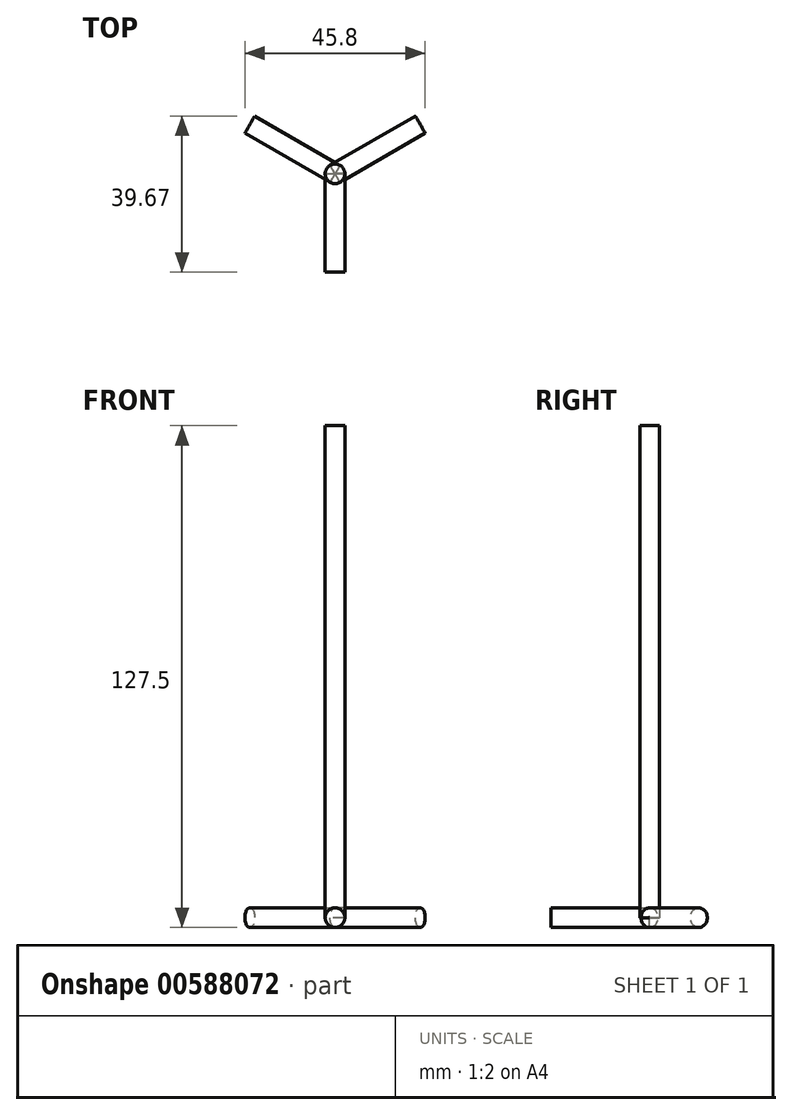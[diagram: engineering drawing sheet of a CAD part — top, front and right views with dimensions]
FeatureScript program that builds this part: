
annotation { "Feature Type Name" : "Feature", "Feature Type Description" : "" }
export const myFeature = defineFeature(function(context is Context, id is Id, definition is map)
    precondition{}
    {
        {
            var Q0;
            Q0=qCreatedBy(makeId("Front.planeOp"),FACE);
            var sketch = newSketch(context, id + "F0", { "sketchPlane" : qUnion([Q0])});
            skCircle(sketch, "E0", {"center": v(0, 0) * mm, "radius": 2.5 * mm});
            skSolve(sketch);
        }
        {
            var Q0;
            Q0 = qSketchRegion(id + "F0", true);
            extrude(context, id + "F1", {"entities" : qUnion([Q0]), "depth" : 25 * mm, "offsetDistance" : 25 * mm});
        }
        {
            var Q0;
            Q0=qCreatedBy(makeId("Top.planeOp"),FACE);
            var sketch = newSketch(context, id + "F2", { "sketchPlane" : qUnion([Q0])});
            skCircle(sketch, "E1", {"center": v(0, 0) * mm, "radius": 2.5 * mm});
            skSolve(sketch);
        }
        {
            var Q0;
            Q0=makeQuery(id+"F1.opExtrude","SWEPT_BODY",BODY,{"disambiguationData":[OSD([sQuery(id+"F0.wireOp",EDGE,"E0")])]});
            var Q1;
            Q1=sQuery(id+"F2.wireOp",EDGE,"E1");
            circularPattern(context, id + "F3", {"entities" : qUnion([Q0]), "axis" : qUnion([Q1]), "angle" : 360 * degree, "instanceCount" : 3, "equalSpace" : true});
        }
        {
            var Q0;
            Q0 = qSketchRegion(id + "F2", true);
            extrude(context, id + "F4", {"entities" : qUnion([Q0]), "depth" : 125 * mm, "offsetDistance" : 25 * mm});
        }
    });
